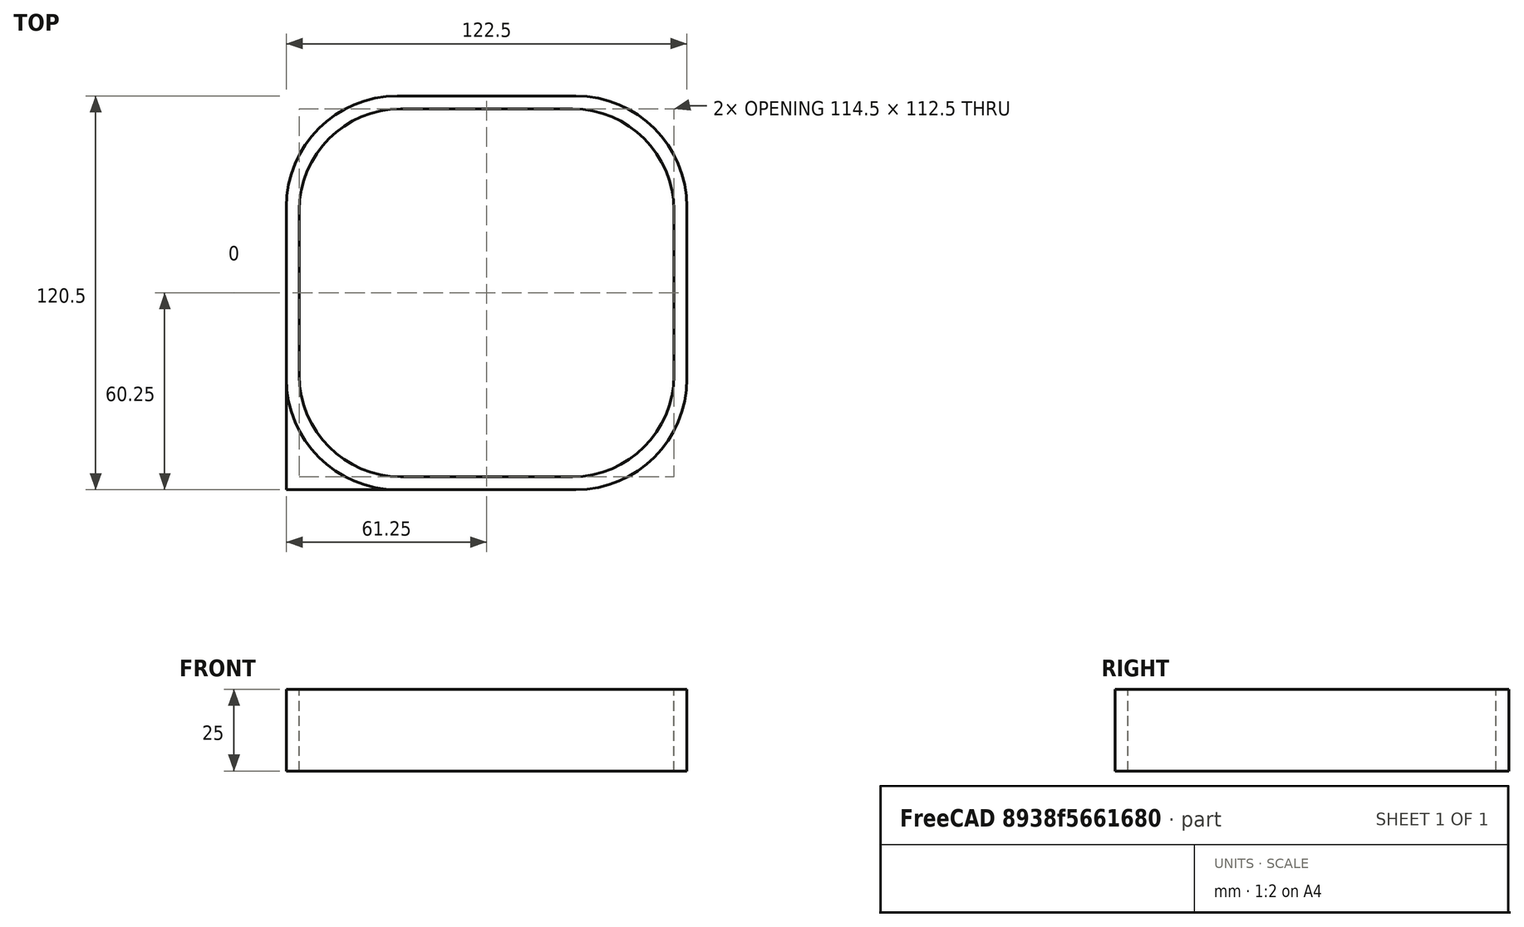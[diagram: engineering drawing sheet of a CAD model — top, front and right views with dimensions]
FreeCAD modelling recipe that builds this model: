
FCSTD DOCUMENT  (FreeCAD 0.14R3703 (Git))
Label: aro_cube_flex
License: CC-BY 3.0
LicenseURL: http://creativecommons.org/licenses/by/3.0/
objects: PartDesign::Fillet×9, Part::Box×2, Part::Cut×1, Part::Feature×1
note: 13 computed .brp shape members not serialized (recipe doc carries the construction recipe); baked Part::Feature solids carry a one-line shape summary decoded from their .brp

FEATURE [Part::Box] Box  label="Cubo"
  Height = 25
  Length = 122.5
  Width = 120.5
FEATURE [Part::Box] Box001  label="Cubo001"
  Height = 32
  Length = 114.5
  Placement = pos=(4,4,0) rot=(0,0,1;0rad)
  Width = 112.5
FEATURE [Part::Cut] Cut
  Base = -> Box
  Tool = -> Box001
FEATURE [PartDesign::Fillet] Fillet
  Base = -> Cut [Edge24]
  Radius = 31
FEATURE [PartDesign::Fillet] Fillet001
  Base = -> Fillet [Edge11]
  Radius = 31
FEATURE [PartDesign::Fillet] Fillet002
  Base = -> Fillet001 [Edge20]
  Radius = 31
FEATURE [PartDesign::Fillet] Fillet003
  Base = -> Fillet002 [Edge19]
  Radius = 31
FEATURE [PartDesign::Fillet] Fillet004
  Base = -> Fillet003 [Edge30]
  Radius = 34
FEATURE [PartDesign::Fillet] Fillet005
  Base = -> Fillet004 [Edge22]
  Radius = 34
FEATURE [PartDesign::Fillet] Fillet006
  Base = -> Fillet005 [Edge22]
  Radius = 34
FEATURE [PartDesign::Fillet] Fillet009
  Base = -> Fillet005 [Edge22]
  Radius = 34
FEATURE [PartDesign::Fillet] Fillet008
  Base = -> Fillet009 [Edge24]
  Radius = 34
FEATURE [Part::Feature] Fillet008001  label="aro_cube_flex"
  shape: bbox 122.5 x 120.5 x 25 mm, 18 faces (baked)
